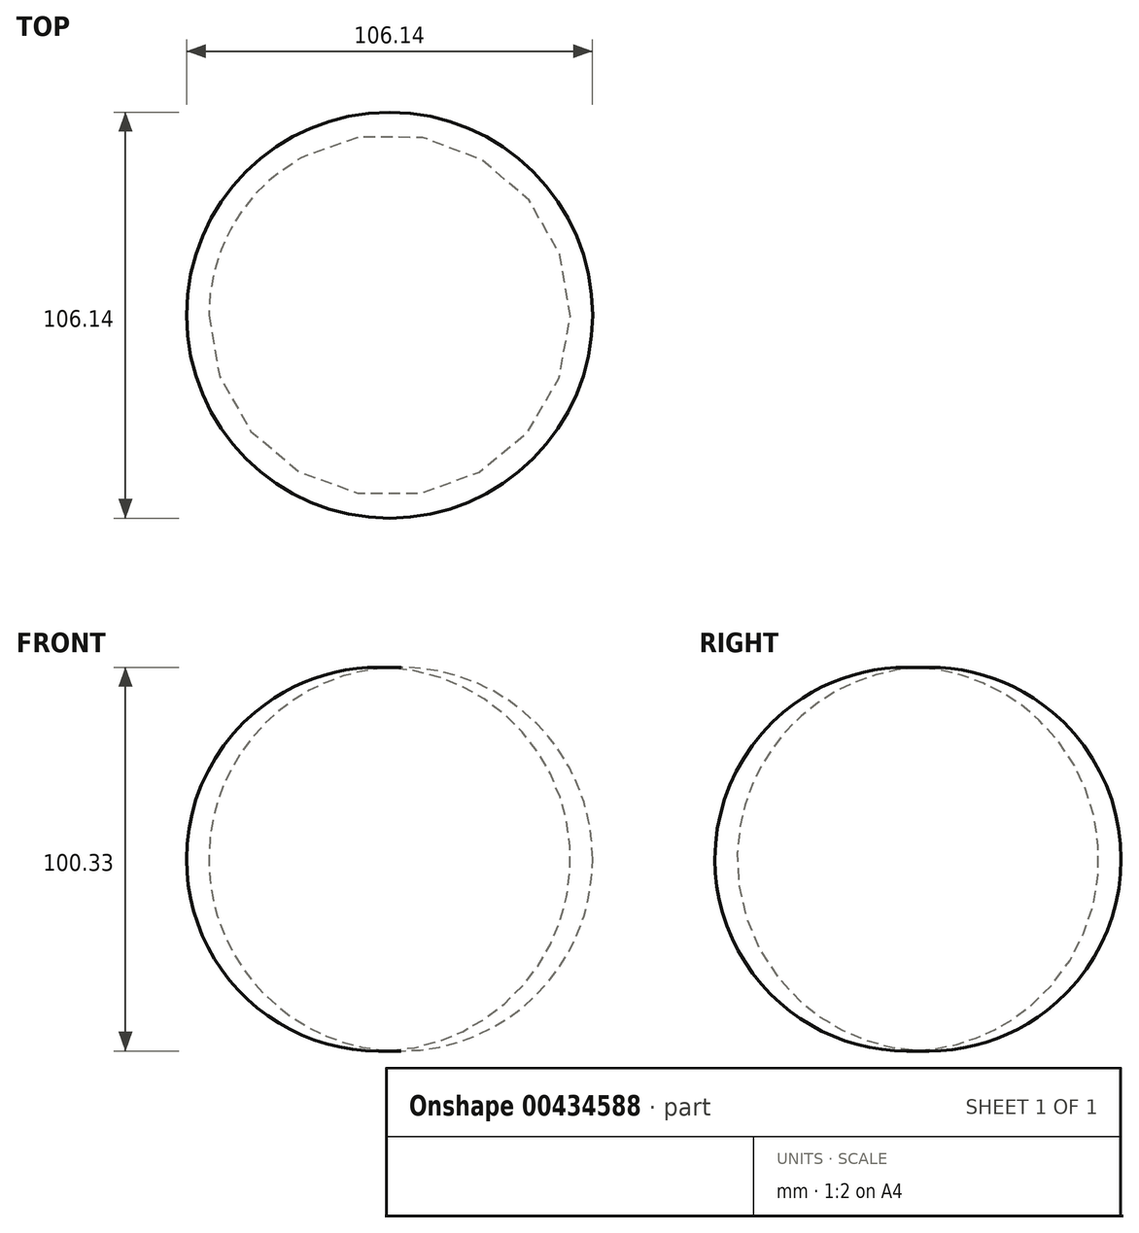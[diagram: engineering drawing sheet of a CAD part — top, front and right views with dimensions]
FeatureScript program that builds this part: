
annotation { "Feature Type Name" : "Feature", "Feature Type Description" : "" }
export const myFeature = defineFeature(function(context is Context, id is Id, definition is map)
    precondition{}
    {
        {
            var Q0;
            Q0=qCreatedBy(makeId("Front.planeOp"),FACE);
            var sketch = newSketch(context, id + "F0", { "sketchPlane" : qUnion([Q0])});
            skLineSegment(sketch, "E0", {"start": v(-44.52, 61.06) * mm, "end": v(-44.52, -39.1) * mm});
            skArc(sketch, "E1", {"start": v(-44.52, -39.1) * mm, "mid": v(8.55, 10.98) * mm, "end": v(-44.52, 61.06) * mm});
            skSolve(sketch);
        }
        {
            var Q0;
            Q0=makeQuery(id+"F0.imprint","IMPRINT",FACE,{"disambiguationData":[TD([[makeQuery(id+"F0.imprint","IMPRINT",EDGE,{"derivedFrom":sQuery(id+"F0.wireOp",EDGE,"E0")}),1.0]])]});
            var Q1;
            Q1=sQuery(id+"F0.wireOp",EDGE,"E0");
            revolve(context, id + "F1", {"entities" : qUnion([Q0]), "axis" : qUnion([Q1]), "revolveType" : RevolveType.FULL});
        }
    });
